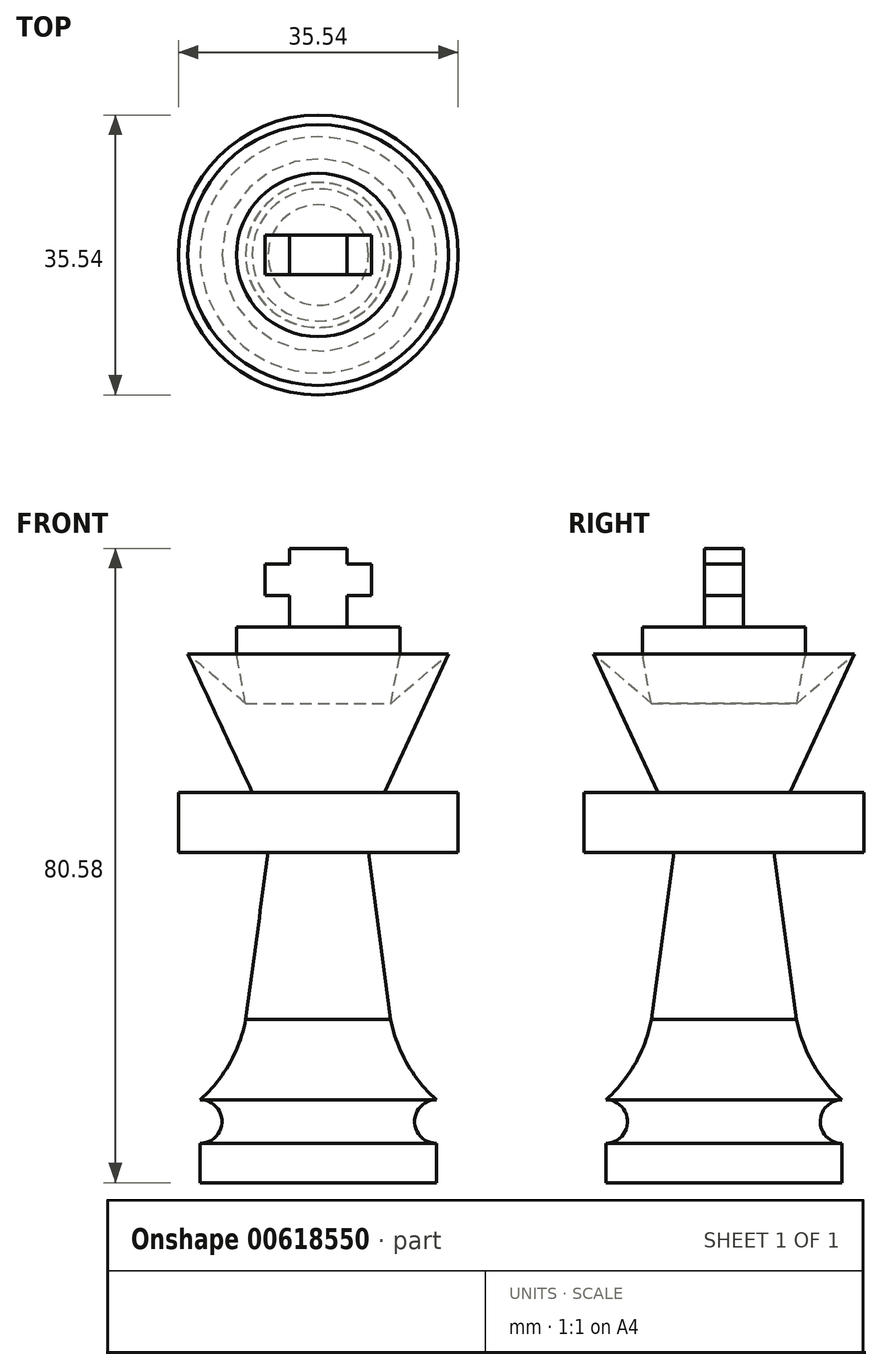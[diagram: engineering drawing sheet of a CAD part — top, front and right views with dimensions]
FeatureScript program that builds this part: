
annotation { "Feature Type Name" : "Feature", "Feature Type Description" : "" }
export const myFeature = defineFeature(function(context is Context, id is Id, definition is map)
    precondition{}
    {
        {
            var Q0;
            Q0=qCreatedBy(makeId("Front.planeOp"),FACE);
            var sketch = newSketch(context, id + "F0", { "sketchPlane" : qUnion([Q0])});
            skLineSegment(sketch, "E0", {"start": v(0, 0) * mm, "end": v(15, 0) * mm});
            skArc(sketch, "E1", {"start": v(15, 5.52) * mm, "mid": v(12.24, 2.76) * mm, "end": v(15, 0) * mm});
            skArc(sketch, "E2", {"start": v(9.2, 15.71) * mm, "mid": v(11.27, 10.15) * mm, "end": v(15, 5.52) * mm});
            skLineSegment(sketch, "E3", {"start": v(9.2, 15.71) * mm, "end": v(6.37, 36.96) * mm});
            skLineSegment(sketch, "E4", {"start": v(6.37, 36.96) * mm, "end": v(17.77, 36.96) * mm});
            skPoint(sketch, "E5.endSnap0", {"position": v(10.37, 42.92) * mm});
            skLineSegment(sketch, "E6", {"start": v(8.39, 44.6) * mm, "end": v(16.57, 62.18) * mm});
            skLineSegment(sketch, "E7", {"start": v(10.37, 65.58) * mm, "end": v(10.37, 62.18) * mm});
            skLineSegment(sketch, "E8", {"start": v(10.37, 65.58) * mm, "end": v(0, 65.58) * mm});
            skLineSegment(sketch, "E9", {"start": v(0, 0) * mm, "end": v(0, 65.58) * mm});
            skPoint(sketch, "E10.orphan", {"position": v(6.37, 42.92) * mm});
            skPoint(sketch, "E11.start.orphan", {"position": v(5.19, 65.58) * mm});
            skLineSegment(sketch, "E12", {"start": v(3.64, 65.58) * mm, "end": v(3.64, 69.58) * mm});
            skLineSegment(sketch, "E13", {"start": v(3.64, 69.58) * mm, "end": v(6.78, 69.58) * mm});
            skLineSegment(sketch, "E14", {"start": v(6.78, 73.58) * mm, "end": v(6.78, 69.58) * mm});
            skLineSegment(sketch, "E15", {"start": v(6.78, 73.58) * mm, "end": v(3.64, 73.58) * mm});
            skLineSegment(sketch, "E16", {"start": v(3.64, 73.58) * mm, "end": v(3.64, 75.58) * mm});
            skLineSegment(sketch, "E17", {"start": v(0, 75.58) * mm, "end": v(3.64, 75.58) * mm});
            skLineSegment(sketch, "E18.MirrorCS", {"start": v(0, 75.58) * mm, "end": v(-3.64, 75.58) * mm});
            skLineSegment(sketch, "E19.MirrorCS", {"start": v(-3.64, 73.58) * mm, "end": v(-3.64, 75.58) * mm});
            skLineSegment(sketch, "E20.MirrorCS", {"start": v(-6.78, 73.58) * mm, "end": v(-3.64, 73.58) * mm});
            skLineSegment(sketch, "E21.MirrorCS", {"start": v(-6.78, 73.58) * mm, "end": v(-6.78, 69.58) * mm});
            skLineSegment(sketch, "E22.MirrorCS", {"start": v(-3.64, 69.58) * mm, "end": v(-6.78, 69.58) * mm});
            skLineSegment(sketch, "E23.MirrorCS", {"start": v(-3.64, 65.58) * mm, "end": v(-3.64, 69.58) * mm});
            skLineSegment(sketch, "E24.MirrorCS", {"start": v(-3.64, 65.58) * mm, "end": v(0, 65.58) * mm});
            skPoint(sketch, "E25.orphan", {"position": v(-10.37, 65.58) * mm});
            skPoint(sketch, "E26.start.orphan", {"position": v(10.37, 48.86) * mm});
            skLineSegment(sketch, "E27", {"start": v(8.39, 44.6) * mm, "end": v(17.77, 44.6) * mm});
            skLineSegment(sketch, "E28", {"start": v(17.77, 36.96) * mm, "end": v(17.77, 44.6) * mm});
            skLineSegment(sketch, "E29", {"start": v(16.57, 62.18) * mm, "end": v(9.24, 55.88) * mm});
            skLineSegment(sketch, "E30", {"start": v(10.37, 62.18) * mm, "end": v(9.24, 55.88) * mm});
            skSolve(sketch);
        }
        {
            var Q0;
            Q0=makeQuery(id+"F0.imprint","IMPRINT",FACE,{"disambiguationData":[TD([[makeQuery(id+"F0.imprint","IMPRINT",EDGE,{"derivedFrom":sQuery(id+"F0.wireOp",EDGE,"E0")}),1.0]])]});
            var Q1;
            Q1=sQuery(id+"F0.wireOp",EDGE,"E9");
            revolve(context, id + "F1", {"entities" : qUnion([Q0]), "axis" : qUnion([Q1]), "revolveType" : RevolveType.FULL});
        }
        {
            var Q0;
            Q0=makeQuery(id+"F1.opRevolve","SWEPT_FACE",FACE,{"disambiguationData":[OSD([sQuery(id+"F0.wireOp",EDGE,"E0")])]});
            extrude(context, id + "F2", {"entities" : qUnion([Q0]), "operationType" : NewBodyOperationType.ADD, "depth" : 5 * mm, "offsetDistance" : 25 * mm});
        }
        {
            var Q0;
            {var subQ2=sQuery(id+"F0.wireOp",EDGE,"E12");Q0=makeQuery(id+"F0.imprint","IMPRINT",FACE,{"disambiguationData":[TD([[makeQuery(id+"F0.imprint","IMPRINT",EDGE,{"derivedFrom":subQ2}),1.0]])]});}
            extrude(context, id + "F3", {"entities" : qUnion([Q0]), "operationType" : NewBodyOperationType.ADD, "depth" : 2.5 * mm, "offsetDistance" : 25 * mm});
        }
        {
            var Q0;
            {var subQ2=sQuery(id+"F0.wireOp",EDGE,"E12");Q0=makeQuery(id+"F0.imprint","IMPRINT",FACE,{"disambiguationData":[TD([[makeQuery(id+"F0.imprint","IMPRINT",EDGE,{"derivedFrom":subQ2}),1.0]])]});}
            extrude(context, id + "F4", {"entities" : qUnion([Q0]), "operationType" : NewBodyOperationType.ADD, "oppositeDirection" : true, "depth" : 2.5 * mm, "offsetDistance" : 25 * mm});
        }
        {
            var Q0;
            Q0=makeQuery(id+"F1.opRevolve","SWEPT_EDGE",EDGE,{"disambiguationData":[OSD([sQuery(id+"F0.wireOp",EDGE,"E7"),sQuery(id+"F0.wireOp",EDGE,"E30")])]});
            fillet(context, id + "F5", {"entities" : qUnion([Q0]), "radius" : 5 * mm, "tangentPropagation" : true, "allowEdgeOverflow" : false});
        }
    });
